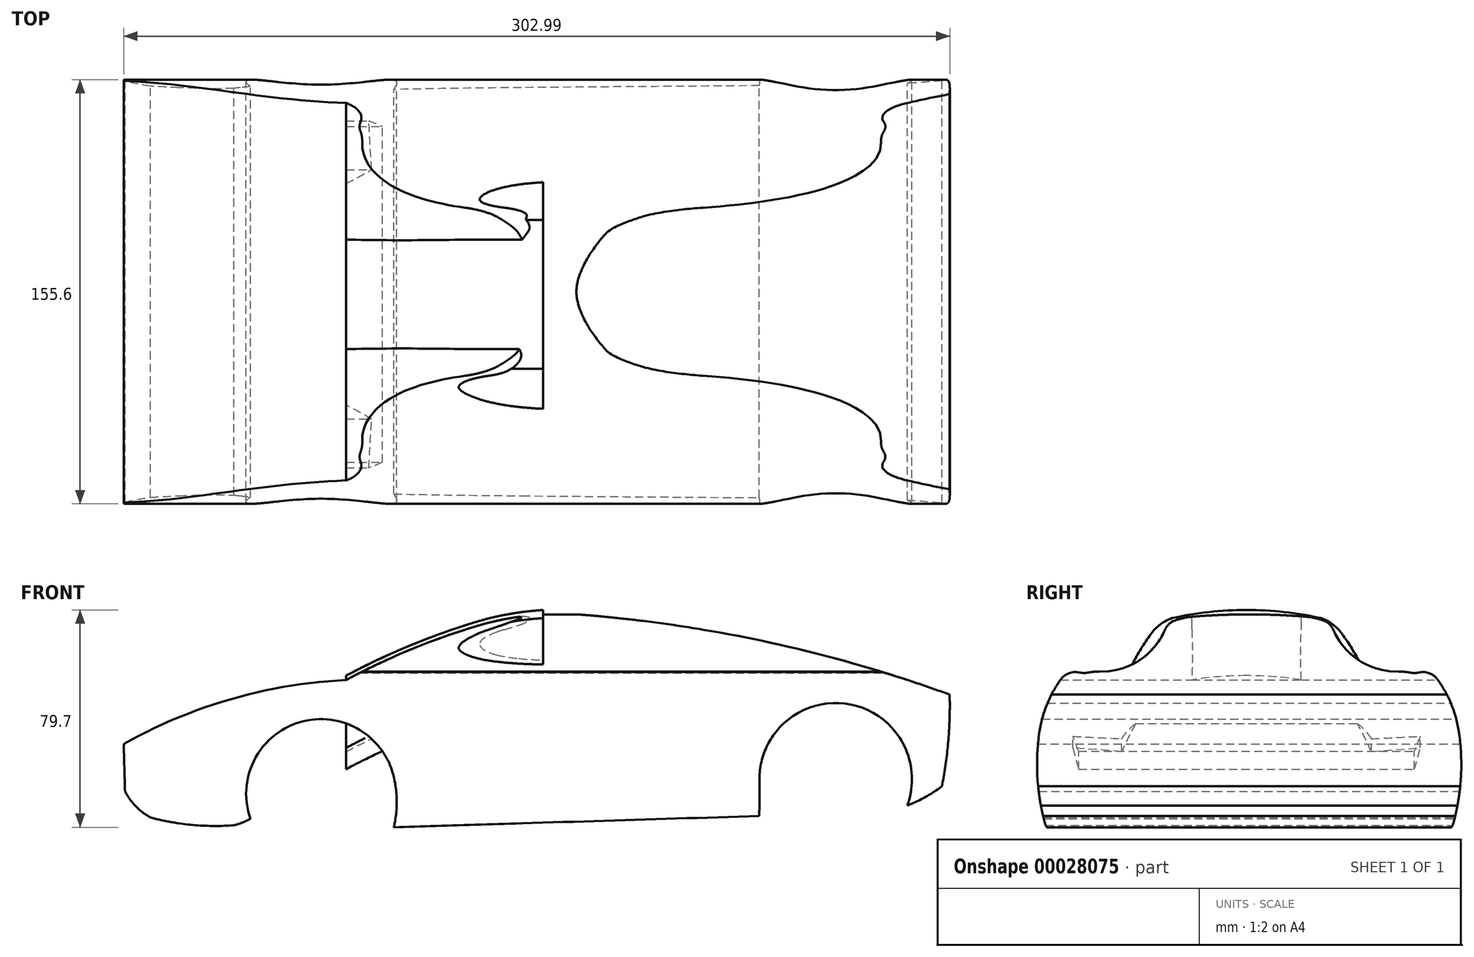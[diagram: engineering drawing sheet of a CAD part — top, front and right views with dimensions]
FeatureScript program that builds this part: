
annotation { "Feature Type Name" : "Feature", "Feature Type Description" : "" }
export const myFeature = defineFeature(function(context is Context, id is Id, definition is map)
    precondition{}
    {
        {
            var Q0;
            Q0=qCreatedBy(makeId("Front.planeOp"),FACE);
            var sketch = newSketch(context, id + "F0", { "sketchPlane" : qUnion([Q0])});
            skArc(sketch, "E0", {"start": v(15.05, 47.41) * mm, "mid": v(-4.75, 47.14) * mm, "end": v(-24.16, 43.2) * mm});
            skArc(sketch, "E1", {"start": v(149.57, 18.13) * mm, "mid": v(83.3, 37.32) * mm, "end": v(15.05, 47.41) * mm});
            skArc(sketch, "E2", {"start": v(167.25, 26.91) * mm, "mid": v(167.05, 27.01) * mm, "end": v(166.85, 27.11) * mm});
            skArc(sketch, "E3", {"start": v(134.01, -22.55) * mm, "mid": v(112.7, 14.62) * mm, "end": v(79.8, -12.82) * mm});
            skArc(sketch, "E4", {"start": v(166.87, 26.7) * mm, "mid": v(166.86, 26.91) * mm, "end": v(166.85, 27.11) * mm});
            skArc(sketch, "E5.trimOffspring", {"start": v(134.01, -22.55) * mm, "mid": v(140.62, -19.48) * mm, "end": v(146.72, -15.5) * mm});
            skArc(sketch, "E6.trimOffspring", {"start": v(146.72, -15.5) * mm, "mid": v(149.07, 1.23) * mm, "end": v(149.57, 18.13) * mm});
            skPoint(sketch, "E7.center.orphan", {"position": v(0, 341.5) * mm});
            skLineSegment(sketch, "E8", {"start": v(79.76, -26.4) * mm, "end": v(79.8, -12.82) * mm});
            skLineSegment(sketch, "E9", {"start": v(-54.28, -30.54) * mm, "end": v(79.76, -26.4) * mm});
            skArc(sketch, "E10", {"start": v(-54.28, -30.54) * mm, "mid": v(-53.22, -21.3) * mm, "end": v(-54.3, -12.05) * mm});
            skArc(sketch, "E11.trimOffspring", {"start": v(-112.97, -29.8) * mm, "mid": v(-109.85, -28.82) * mm, "end": v(-106.9, -27.4) * mm});
            skArc(sketch, "E12.trimOffspring", {"start": v(-143.62, -26.94) * mm, "mid": v(-128.41, -29.66) * mm, "end": v(-112.97, -29.8) * mm});
            skArc(sketch, "E13", {"start": v(-152.88, -17.4) * mm, "mid": v(-148.93, -22.83) * mm, "end": v(-143.62, -26.94) * mm});
            skLineSegment(sketch, "E14", {"start": v(-153.37, 0) * mm, "end": v(-152.88, -17.4) * mm});
            skArc(sketch, "E15.trimOffspring", {"start": v(-71.76, 23.52) * mm, "mid": v(-113.93, 16.5) * mm, "end": v(-153.37, 0) * mm});
            skArc(sketch, "E16.trimOffspring", {"start": v(-24.16, 43.2) * mm, "mid": v(-48.45, 34.54) * mm, "end": v(-71.76, 23.52) * mm});
            skArc(sketch, "E17.trimOffspring", {"start": v(166.87, 26.7) * mm, "mid": v(167.06, 26.81) * mm, "end": v(167.25, 26.91) * mm});
            skArc(sketch, "E18.converted", {"start": v(-54.3, -12.05) * mm, "mid": v(-88.7, 8.04) * mm, "end": v(-106.9, -27.4) * mm});
            skSolve(sketch);
        }
        {
            var Q0;
            Q0=makeQuery(id+"F0.imprint","IMPRINT",FACE,{"disambiguationData":[TD([[makeQuery(id+"F0.imprint","IMPRINT",EDGE,{"derivedFrom":sQuery(id+"F0.wireOp",EDGE,"E0")}),1.0]])]});
            extrude(context, id + "F1", {"entities" : qUnion([Q0]), "depth" : 159.1 * mm});
        }
        {
            var Q0;
            Q0=qCreatedBy(makeId("Right.planeOp"),FACE);
            var sketch = newSketch(context, id + "F2", { "sketchPlane" : qUnion([Q0])});
            skArc(sketch, "E19", {"start": v(-134.42, 26.57) * mm, "mid": v(-120.03, 30.58) * mm, "end": v(-110.38, 41.98) * mm});
            skLineSegment(sketch, "E20", {"start": v(-79.54, 87.2) * mm, "end": v(-79.56, -93.7) * mm, "construction": true});
            skPoint(sketch, "E20.startSnap0", {"position": v(-79.54, 47.41) * mm});
            skArc(sketch, "E21", {"start": v(-107.11, 45.19) * mm, "mid": v(-109.07, 43.91) * mm, "end": v(-110.38, 41.98) * mm});
            skArc(sketch, "E22.trimOffspring", {"start": v(-79.55, 47.57) * mm, "mid": v(-90.2, 47.35) * mm, "end": v(-100.84, 46.68) * mm});
            skArc(sketch, "E23.trimOffspring", {"start": v(-100.84, 46.68) * mm, "mid": v(-104.03, 46.17) * mm, "end": v(-107.11, 45.19) * mm});
            skArc(sketch, "E24", {"start": v(-134.42, 26.57) * mm, "mid": v(-136.5, 26.5) * mm, "end": v(-138.55, 26.23) * mm});
            skArc(sketch, "E25", {"start": v(-141.9, 26.27) * mm, "mid": v(-140.23, 26.08) * mm, "end": v(-138.55, 26.23) * mm});
            skArc(sketch, "E26", {"start": v(-141.9, 26.27) * mm, "mid": v(-145.67, 25.99) * mm, "end": v(-148.66, 23.69) * mm});
            skArc(sketch, "E27", {"start": v(-148.66, 23.69) * mm, "mid": v(-153.73, 14.5) * mm, "end": v(-156.48, 4.37) * mm});
            skArc(sketch, "E28", {"start": v(-154.44, -29.09) * mm, "mid": v(-152.48, -31.8) * mm, "end": v(-149.22, -32.54) * mm});
            skLineSegment(sketch, "E29", {"start": v(-150.49, -32.54) * mm, "end": v(-79.55, -32.54) * mm});
            skArc(sketch, "E30.trimOffspring", {"start": v(-156.48, 4.37) * mm, "mid": v(-157.2, -12.47) * mm, "end": v(-154.44, -29.09) * mm});
            skArc(sketch, "E31.MirrorCS", {"start": v(-24.68, 26.56) * mm, "mid": v(-22.6, 26.5) * mm, "end": v(-20.55, 26.22) * mm});
            skArc(sketch, "E32.MirrorCS", {"start": v(-17.2, 26.26) * mm, "mid": v(-18.87, 26.07) * mm, "end": v(-20.55, 26.22) * mm});
            skArc(sketch, "E33.MirrorCS", {"start": v(-51.98, 45.19) * mm, "mid": v(-50.03, 43.9) * mm, "end": v(-48.71, 41.98) * mm});
            skArc(sketch, "E34.MirrorCS", {"start": v(-17.2, 26.26) * mm, "mid": v(-13.43, 25.98) * mm, "end": v(-10.44, 23.68) * mm});
            skArc(sketch, "E35.MirrorCS", {"start": v(-4.66, -29.1) * mm, "mid": v(-6.62, -31.8) * mm, "end": v(-9.88, -32.55) * mm});
            skArc(sketch, "E36.MirrorCS", {"start": v(-58.26, 46.68) * mm, "mid": v(-55.06, 46.17) * mm, "end": v(-51.98, 45.19) * mm});
            skLineSegment(sketch, "E37.MirrorCS", {"start": v(-8.62, -32.55) * mm, "end": v(-79.55, -32.54) * mm});
            skPoint(sketch, "E38.MirrorP", {"position": v(-79.55, 47.41) * mm});
            skArc(sketch, "E39.MirrorCS", {"start": v(-2.62, 4.36) * mm, "mid": v(-1.9, -12.48) * mm, "end": v(-4.66, -29.1) * mm});
            skArc(sketch, "E40.MirrorCS", {"start": v(-10.44, 23.68) * mm, "mid": v(-5.37, 14.49) * mm, "end": v(-2.62, 4.36) * mm});
            skArc(sketch, "E41.MirrorCS", {"start": v(-79.55, 47.57) * mm, "mid": v(-68.9, 47.35) * mm, "end": v(-58.26, 46.68) * mm});
            skArc(sketch, "E42.MirrorCS", {"start": v(-24.68, 26.56) * mm, "mid": v(-39.07, 30.57) * mm, "end": v(-48.71, 41.98) * mm});
            skLineSegment(sketch, "E43.MirrorCS", {"start": v(-88.63, 47.41) * mm, "end": v(-70.54, 47.41) * mm});
            skLineSegment(sketch, "E44.bottom", {"start": v(-190.26, 85.25) * mm, "end": v(35.36, 85.25) * mm});
            skLineSegment(sketch, "E44.top", {"start": v(-190.26, -80) * mm, "end": v(35.36, -80) * mm});
            skLineSegment(sketch, "E44.left", {"start": v(-190.26, 85.25) * mm, "end": v(-190.26, -80) * mm});
            skLineSegment(sketch, "E44.right", {"start": v(35.36, 85.25) * mm, "end": v(35.36, -80) * mm});
            skSolve(sketch);
        }
        {
            var Q0;
            Q0=makeQuery(id+"F2.imprint","IMPRINT",FACE,{"disambiguationData":[TD([[makeQuery(id+"F2.imprint","IMPRINT",EDGE,{"derivedFrom":sQuery(id+"F2.wireOp",EDGE,"E19")}),1.0]])]});
            extrude(context, id + "F3", {"entities" : qUnion([Q0]), "operationType" : NewBodyOperationType.REMOVE, "endBound" : BoundingType.THROUGH_ALL, "oppositeDirection" : true, "depth" : 25.4 * mm, "hasSecondDirection" : true, "secondDirectionBound" : SecondDirectionBoundingType.THROUGH_ALL, "secondDirectionOppositeDirection" : false, "secondDirectionDepth" : 25.4 * mm});
        }
        {
            var Q0;
            Q0=qCreatedBy(makeId("Top.planeOp"),FACE);
            var sketch = newSketch(context, id + "F4", { "sketchPlane" : qUnion([Q0])});
            skLineSegment(sketch, "E45", {"start": v(-173.45, -79.89) * mm, "end": v(167.36, -79.89) * mm, "construction": true});
            skPoint(sketch, "E45.startSnap0", {"position": v(6.6, -79.89) * mm});
            skLineSegment(sketch, "E46", {"start": v(6.6, -65.86) * mm, "end": v(6.6, -92.45) * mm, "construction": true});
            skEllipticalArc(sketch, "E47", {});
            skLineSegment(sketch, "E48", {"start": v(6.6, 32.06) * mm, "end": v(6.6, -172.68) * mm, "construction": true});
            skEllipticalArc(sketch, "E49.MirrorCS", {});
            skLineSegment(sketch, "E50", {"start": v(-103.1, -79.89) * mm, "end": v(116.3, -79.89) * mm});
            const initialGuessF4  = {"E47": [0.006603998132050037, -0.07988565415143967, -1, 0, 0.10970037392830895, 0.05524768441884324, 3.141592653589793, 4.71238898038469], "E49.MirrorCS": [0.006603998132050037, -0.07988565415143967, 1, 0, 0.10970037392830895, 0.05524768441884324, 1.5707963267948966, 3.141592653589793], "E49.MirrorCS": [0.006603998132050037, -0.07988565415143967, 1, 0, 0.10970037392830895, 0.05524768441884324, 1.5707963267948966, 3.141592653589793]};
            skSetInitialGuess(sketch, initialGuessF4);
            skSolve(sketch);
        }
        {
            var Q0;
            Q0=qCreatedBy(makeId("Top.planeOp"),FACE);
            var sketch = newSketch(context, id + "F5", { "sketchPlane" : qUnion([Q0])});
            skLineSegment(sketch, "E51.0", {"start": v(-173.45, -79.89) * mm, "end": v(167.36, -79.89) * mm, "construction": true});
            skLineSegment(sketch, "E52", {"start": v(-168.51, -79.89) * mm, "end": v(159.73, -79.89) * mm, "construction": true});
            skSolve(sketch);
        }
        {
            var Q0;
            Q0=qCreatedBy(makeId("Right.planeOp"),FACE);
            var sketch = newSketch(context, id + "F6", { "sketchPlane" : qUnion([Q0])});
            skArc(sketch, "E53", {"start": v(-115.63, 40.3) * mm, "mid": v(-121.47, 31.05) * mm, "end": v(-126.3, 21.24) * mm});
            skArc(sketch, "E54", {"start": v(-103.73, 47) * mm, "mid": v(-110.43, 44.99) * mm, "end": v(-115.63, 40.3) * mm});
            skArc(sketch, "E55", {"start": v(-80.52, 49.13) * mm, "mid": v(-94.25, 48.4) * mm, "end": v(-107.83, 46.16) * mm});
            skLineSegment(sketch, "E56", {"start": v(-80.52, 122.2) * mm, "end": v(-80.52, 122.2) * mm});
            skPoint(sketch, "E56.endSnap0", {"position": v(-80.52, 122.2) * mm});
            skLineSegment(sketch, "E57", {"start": v(-80.52, -38.84) * mm, "end": v(-80.52, 59.98) * mm, "construction": true});
            skLineSegment(sketch, "E58", {"start": v(-126.3, 21.24) * mm, "end": v(-144.2, 22.63) * mm});
            skLineSegment(sketch, "E59", {"start": v(-144.2, 22.63) * mm, "end": v(-142.1, 14.83) * mm});
            skLineSegment(sketch, "E60", {"start": v(-142.1, 14.83) * mm, "end": v(-80.52, 14.83) * mm});
            skLineSegment(sketch, "E61.MirrorCS", {"start": v(-16.83, 22.63) * mm, "end": v(-18.93, 14.83) * mm});
            skLineSegment(sketch, "E62.MirrorCS", {"start": v(-34.74, 21.24) * mm, "end": v(-16.83, 22.63) * mm});
            skArc(sketch, "E63.MirrorCS", {"start": v(-80.52, 49.13) * mm, "mid": v(-66.78, 48.4) * mm, "end": v(-53.2, 46.16) * mm});
            skArc(sketch, "E64.MirrorCS", {"start": v(-57.3, 47) * mm, "mid": v(-50.6, 44.99) * mm, "end": v(-45.4, 40.3) * mm});
            skArc(sketch, "E65.MirrorCS", {"start": v(-45.4, 40.3) * mm, "mid": v(-39.57, 31.05) * mm, "end": v(-34.74, 21.24) * mm});
            skLineSegment(sketch, "E66.MirrorCS", {"start": v(-18.93, 14.83) * mm, "end": v(-80.52, 14.83) * mm});
            skSolve(sketch);
        }
        {
            var Q0;
            Q0=qCreatedBy(makeId("Front.planeOp"),FACE);
            var sketch = newSketch(context, id + "F7", { "sketchPlane" : qUnion([Q0])});
            skArc(sketch, "E67.0", {"start": v(0.52, 47.57) * mm, "mid": v(-3.96, 47.22) * mm, "end": v(-8.43, 46.68) * mm});
            skArc(sketch, "E68.0", {"start": v(-8.43, 46.68) * mm, "mid": v(-12.53, 46.01) * mm, "end": v(-16.6, 45.19) * mm});
            skArc(sketch, "E69.0", {"start": v(-16.6, 45.19) * mm, "mid": v(-20.4, 44.27) * mm, "end": v(-24.16, 43.2) * mm});
            skArc(sketch, "E70.0", {"start": v(-24.16, 43.2) * mm, "mid": v(-26.13, 42.6) * mm, "end": v(-28.1, 41.98) * mm});
            skArc(sketch, "E71.0", {"start": v(-71.76, 23.52) * mm, "mid": v(-109.43, 17.74) * mm, "end": v(-145.13, 4.37) * mm});
            skArc(sketch, "E72.0", {"start": v(-145.13, 4.37) * mm, "mid": v(-149.28, 2.23) * mm, "end": v(-153.37, 0) * mm});
            skArc(sketch, "E73", {"start": v(-28.1, 41.98) * mm, "mid": v(-50.34, 33.72) * mm, "end": v(-71.76, 23.52) * mm});
            skSolve(sketch);
        }
        {
            var Q0;
            {var subQ9=sQuery(id+"F6.wireOp",EDGE,"E53");Q0=makeQuery(id+"F6.imprint","IMPRINT",FACE,{"disambiguationData":[TD([[makeQuery(id+"F6.imprint","IMPRINT",EDGE,{"derivedFrom":subQ9}),1.0]])]});}
            var Q1;
            Q1=sQuery(id+"F7.wireOp",EDGE,"E67.0");
            var Q2;
            Q2=sQuery(id+"F7.wireOp",EDGE,"E68.0");
            var Q3;
            Q3=sQuery(id+"F7.wireOp",EDGE,"E69.0");
            var Q4;
            Q4=sQuery(id+"F7.wireOp",EDGE,"E70.0");
            var Q5;
            Q5=sQuery(id+"F7.wireOp",EDGE,"E73");
            sweep(context, id + "F8", {"operationType" : NewBodyOperationType.ADD, "profiles" : qUnion([Q0]), "path" : qUnion([Q1, Q2, Q3, Q4, Q5]), "keepProfileOrientation" : true});
        }
    });
